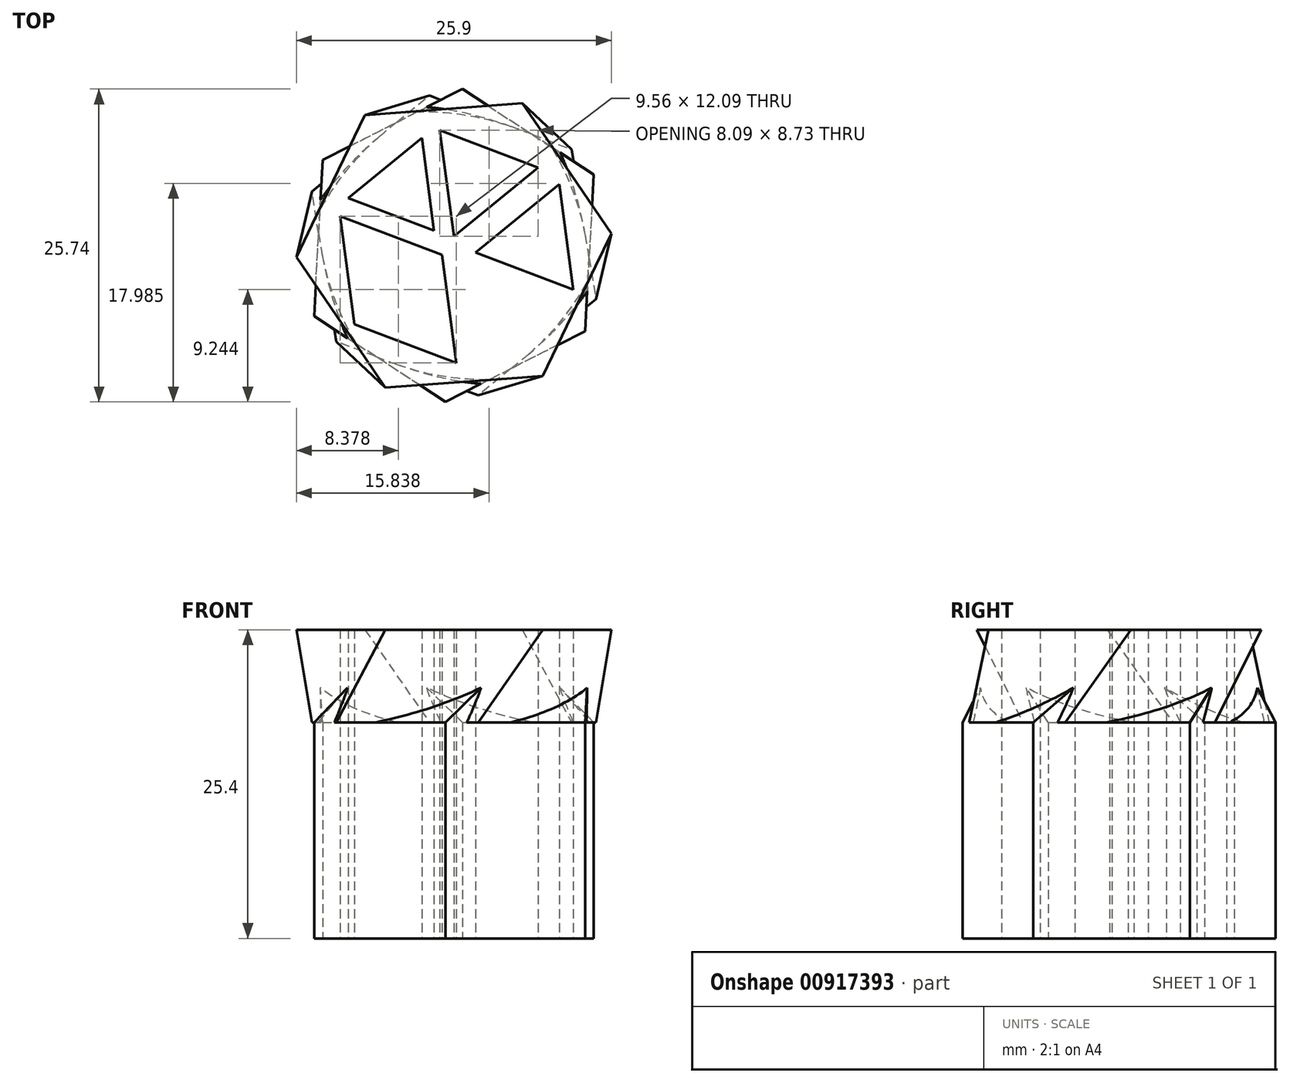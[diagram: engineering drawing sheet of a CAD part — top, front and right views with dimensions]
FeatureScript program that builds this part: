
annotation { "Feature Type Name" : "Feature", "Feature Type Description" : "" }
export const myFeature = defineFeature(function(context is Context, id is Id, definition is map)
    precondition{}
    {
        {
            var Q0;
            Q0=qCreatedBy(makeId("Top.planeOp"),FACE);
            cPlane(context, id + "F0", {"entities" : qUnion([Q0]), "cplaneType" : CPlaneType.OFFSET, "offset" : 7.62 * mm, "width" : 152.4 * mm, "height" : 152.4 * mm});
        }
        {
            var Q0;
            Q0=qCreatedBy(makeId("Top.planeOp"),FACE);
            var sketch = newSketch(context, id + "F1", { "sketchPlane" : qUnion([Q0])});
            skCircle(sketch, "E0.cCircle", {"center": v(0, 0) * mm, "radius": 10.82 * mm, "construction": true});
            skLineSegment(sketch, "E0.0", {"start": v(-11.68, 4.43) * mm, "end": v(-2, 12.33) * mm});
            skLineSegment(sketch, "E0.1", {"start": v(-2, 12.33) * mm, "end": v(9.68, 7.9) * mm});
            skLineSegment(sketch, "E0.2", {"start": v(9.68, 7.9) * mm, "end": v(11.68, -4.43) * mm});
            skLineSegment(sketch, "E0.3", {"start": v(11.68, -4.43) * mm, "end": v(2, -12.33) * mm});
            skLineSegment(sketch, "E0.4", {"start": v(2, -12.33) * mm, "end": v(-9.68, -7.9) * mm});
            skLineSegment(sketch, "E0.5", {"start": v(-9.68, -7.9) * mm, "end": v(-11.68, 4.43) * mm});
            skPoint(sketch, "E0.0.midPoint", {"position": v(-6.84, 8.38) * mm});
            skSolve(sketch);
        }
        {
            var Q0;
            Q0=qCreatedBy(id+"F0.planeOp",FACE);
            var sketch = newSketch(context, id + "F2", { "sketchPlane" : qUnion([Q0])});
            skCircle(sketch, "E1.cCircle", {"center": v(0, 0) * mm, "radius": 11.24 * mm, "construction": true});
            skLineSegment(sketch, "E1.0", {"start": v(5.63, 11.7) * mm, "end": v(12.95, 0.97) * mm});
            skLineSegment(sketch, "E1.1", {"start": v(12.95, 0.97) * mm, "end": v(7.31, -10.73) * mm});
            skLineSegment(sketch, "E1.2", {"start": v(7.31, -10.73) * mm, "end": v(-5.63, -11.7) * mm});
            skLineSegment(sketch, "E1.3", {"start": v(-5.63, -11.7) * mm, "end": v(-12.95, -0.97) * mm});
            skLineSegment(sketch, "E1.4", {"start": v(-12.95, -0.97) * mm, "end": v(-7.31, 10.73) * mm});
            skLineSegment(sketch, "E1.5", {"start": v(-7.31, 10.73) * mm, "end": v(5.63, 11.7) * mm});
            skPoint(sketch, "E1.0.midPoint", {"position": v(9.3, 6.33) * mm});
            skSolve(sketch);
        }
        {
            var Q0;
            Q0=makeQuery(id+"F2.imprint","IMPRINT",FACE,{"disambiguationData":[TD([[makeQuery(id+"F2.imprint","IMPRINT",EDGE,{"derivedFrom":sQuery(id+"F2.wireOp",EDGE,"E1.0")}),-1.0]])]});
            var Q1;
            Q1=makeQuery(id+"F1.imprint","IMPRINT",FACE,{"disambiguationData":[TD([[makeQuery(id+"F1.imprint","IMPRINT",EDGE,{"derivedFrom":sQuery(id+"F1.wireOp",EDGE,"E0.0")}),-1.0]])]});
            loft(context, id + "F3", {"sheetProfilesArray" : [{ "sheetProfileEntities" : qUnion([Q0]) }, { "sheetProfileEntities" : qUnion([Q1]) }]});
        }
        {
            var Q0;
            Q0=makeQuery(id+"F1.imprint","IMPRINT",FACE,{"disambiguationData":[TD([[makeQuery(id+"F1.imprint","IMPRINT",EDGE,{"derivedFrom":sQuery(id+"F1.wireOp",EDGE,"E0.0")}),-1.0]])]});
            var sketch = newSketch(context, id + "F4", { "sketchPlane" : qUnion([Q0])});
            skLineSegment(sketch, "E2", {"start": v(-8.17, -6.5) * mm, "end": v(1.78, -10.27) * mm, "construction": true});
            skLineSegment(sketch, "E3", {"start": v(1.78, -10.27) * mm, "end": v(9.82, -3.7) * mm, "construction": true});
            skLineSegment(sketch, "E4", {"start": v(9.82, -3.7) * mm, "end": v(8.56, 5.8) * mm, "construction": true});
            skLineSegment(sketch, "E5", {"start": v(8.56, 5.8) * mm, "end": v(-1.65, 9.67) * mm, "construction": true});
            skLineSegment(sketch, "E6", {"start": v(-1.65, 9.67) * mm, "end": v(-9.47, 3.28) * mm, "construction": true});
            skLineSegment(sketch, "E7", {"start": v(-9.47, 3.28) * mm, "end": v(-8.17, -6.5) * mm, "construction": true});
            skLineSegment(sketch, "E8", {"start": v(-9.35, 2.42) * mm, "end": v(-0.97, -0.76) * mm});
            skLineSegment(sketch, "E9", {"start": v(-0.97, -0.76) * mm, "end": v(0.2, -9.67) * mm});
            skLineSegment(sketch, "E10", {"start": v(-9.35, 2.42) * mm, "end": v(-8.17, -6.5) * mm});
            skLineSegment(sketch, "E11", {"start": v(0.2, -9.67) * mm, "end": v(-8.17, -6.5) * mm});
            skLineSegment(sketch, "E12", {"start": v(-8.7, 3.9) * mm, "end": v(-1.63, 1.22) * mm});
            skLineSegment(sketch, "E13", {"start": v(-1.63, 1.22) * mm, "end": v(-2.64, 8.85) * mm});
            skLineSegment(sketch, "E14", {"start": v(-2.64, 8.85) * mm, "end": v(-8.7, 3.9) * mm});
            skLineSegment(sketch, "E15", {"start": v(6.93, 6.41) * mm, "end": v(0, 0.75) * mm});
            skLineSegment(sketch, "E16", {"start": v(0, 0.75) * mm, "end": v(-1.16, 9.48) * mm});
            skLineSegment(sketch, "E17", {"start": v(-1.16, 9.48) * mm, "end": v(6.93, 6.41) * mm});
            skLineSegment(sketch, "E18", {"start": v(8.66, 5.03) * mm, "end": v(1.78, -0.59) * mm});
            skLineSegment(sketch, "E19", {"start": v(1.78, -0.59) * mm, "end": v(9.8, -3.63) * mm});
            skLineSegment(sketch, "E20", {"start": v(9.8, -3.63) * mm, "end": v(8.66, 5.03) * mm});
            skLineSegment(sketch, "E21", {"start": v(0.66, -1.8) * mm, "end": v(1.78, -10.27) * mm});
            skLineSegment(sketch, "E22", {"start": v(1.78, -10.27) * mm, "end": v(0.66, -1.8) * mm});
            skLineSegment(sketch, "E23", {"start": v(0.66, -1.8) * mm, "end": v(8.51, -4.77) * mm});
            skLineSegment(sketch, "E24", {"start": v(8.51, -4.77) * mm, "end": v(1.78, -10.27) * mm});
            skSolve(sketch);
        }
        {
            var Q0;
            Q0=makeQuery(id+"F4.imprint","IMPRINT",FACE,{"disambiguationData":[TD([[makeQuery(id+"F4.imprint","IMPRINT",EDGE,{"derivedFrom":sQuery(id+"F4.wireOp",EDGE,"E22")}),-1.0]])]});
            var Q1;
            Q1=makeQuery(id+"F4.imprint","IMPRINT",FACE,{"disambiguationData":[TD([[makeQuery(id+"F4.imprint","IMPRINT",EDGE,{"derivedFrom":sQuery(id+"F4.wireOp",EDGE,"E8")}),-1.0]])]});
            var Q2;
            Q2=makeQuery(id+"F4.imprint","IMPRINT",FACE,{"disambiguationData":[TD([[makeQuery(id+"F4.imprint","IMPRINT",EDGE,{"derivedFrom":sQuery(id+"F4.wireOp",EDGE,"E12")}),1.0]])]});
            var Q3;
            Q3=makeQuery(id+"F4.imprint","IMPRINT",FACE,{"disambiguationData":[TD([[makeQuery(id+"F4.imprint","IMPRINT",EDGE,{"derivedFrom":sQuery(id+"F4.wireOp",EDGE,"E15")}),-1.0]])]});
            var Q4;
            Q4=makeQuery(id+"F4.imprint","IMPRINT",FACE,{"disambiguationData":[TD([[makeQuery(id+"F4.imprint","IMPRINT",EDGE,{"derivedFrom":sQuery(id+"F4.wireOp",EDGE,"E18")}),1.0]])]});
            extrude(context, id + "F5", {"entities" : qUnion([Q0, Q1, Q2, Q3, Q4]), "operationType" : NewBodyOperationType.REMOVE, "endBound" : BoundingType.THROUGH_ALL, "depth" : 25.4 * mm, "offsetDistance" : 25.4 * mm});
        }
        {
            var Q0;
            Q0=qCreatedBy(makeId("Top.planeOp"),FACE);
            cPlane(context, id + "F6", {"entities" : qUnion([Q0]), "cplaneType" : CPlaneType.OFFSET, "offset" : 17.78 * mm, "oppositeDirection" : true, "width" : 152.4 * mm, "height" : 152.4 * mm});
        }
        {
            var Q0;
            Q0=qCreatedBy(id+"F6.planeOp",FACE);
            var sketch = newSketch(context, id + "F7", { "sketchPlane" : qUnion([Q0])});
            skCircle(sketch, "E25.cCircle", {"center": v(0, 0) * mm, "radius": 11.17 * mm, "construction": true});
            skLineSegment(sketch, "E25.0", {"start": v(-10.8, 7.05) * mm, "end": v(0.7, 12.87) * mm});
            skLineSegment(sketch, "E25.1", {"start": v(0.7, 12.87) * mm, "end": v(11.5, 5.83) * mm});
            skLineSegment(sketch, "E25.2", {"start": v(11.5, 5.83) * mm, "end": v(10.8, -7.05) * mm});
            skLineSegment(sketch, "E25.3", {"start": v(10.8, -7.05) * mm, "end": v(-0.7, -12.87) * mm});
            skLineSegment(sketch, "E25.4", {"start": v(-0.7, -12.87) * mm, "end": v(-11.5, -5.83) * mm});
            skLineSegment(sketch, "E25.5", {"start": v(-11.5, -5.83) * mm, "end": v(-10.8, 7.05) * mm});
            skPoint(sketch, "E25.0.midPoint", {"position": v(-5.05, 9.96) * mm});
            skSolve(sketch);
        }
        {
            var Q0;
            Q0=makeQuery(id+"F7.imprint","IMPRINT",FACE,{"disambiguationData":[TD([[makeQuery(id+"F7.imprint","IMPRINT",EDGE,{"derivedFrom":sQuery(id+"F7.wireOp",EDGE,"E25.0")}),-1.0]])]});
            extrude(context, id + "F8", {"entities" : qUnion([Q0]), "operationType" : NewBodyOperationType.ADD, "depth" : 22.86 * mm, "offsetDistance" : 25.4 * mm});
        }
        {
            var Q0;
            Q0=makeQuery(id+"F8.boolean.opBoolean","SPLIT",FACE,{"disambiguationData":[TD([makeQuery(id+"F5.boolean.opBoolean","COPY",FACE,{"derivedFrom":makeQuery(id+"F5.opExtrude","SWEPT_FACE",FACE,{"disambiguationData":[OSD([sQuery(id+"F4.wireOp",EDGE,"E8")])]})})])],"derivedFrom":makeQuery(id+"F8.opExtrude","CAP_FACE",FACE,{"disambiguationData":[OSD([sQuery(id+"F7.wireOp",EDGE,"E25.0"),sQuery(id+"F7.wireOp",EDGE,"E25.1"),sQuery(id+"F7.wireOp",EDGE,"E25.2"),sQuery(id+"F7.wireOp",EDGE,"E25.3"),sQuery(id+"F7.wireOp",EDGE,"E25.4"),sQuery(id+"F7.wireOp",EDGE,"E25.5")])],"isStart":false})});
            var Q1;
            Q1=makeQuery(id+"F8.boolean.opBoolean","SPLIT",FACE,{"disambiguationData":[TD([makeQuery(id+"F5.boolean.opBoolean","COPY",FACE,{"derivedFrom":makeQuery(id+"F5.opExtrude","SWEPT_FACE",FACE,{"disambiguationData":[OSD([sQuery(id+"F4.wireOp",EDGE,"E12")])]})})])],"derivedFrom":makeQuery(id+"F8.opExtrude","CAP_FACE",FACE,{"disambiguationData":[OSD([sQuery(id+"F7.wireOp",EDGE,"E25.0"),sQuery(id+"F7.wireOp",EDGE,"E25.1"),sQuery(id+"F7.wireOp",EDGE,"E25.2"),sQuery(id+"F7.wireOp",EDGE,"E25.3"),sQuery(id+"F7.wireOp",EDGE,"E25.4"),sQuery(id+"F7.wireOp",EDGE,"E25.5")])],"isStart":false})});
            var Q2;
            Q2=makeQuery(id+"F8.boolean.opBoolean","SPLIT",FACE,{"disambiguationData":[TD([makeQuery(id+"F5.boolean.opBoolean","COPY",FACE,{"derivedFrom":makeQuery(id+"F5.opExtrude","SWEPT_FACE",FACE,{"disambiguationData":[OSD([sQuery(id+"F4.wireOp",EDGE,"E15")])]})})])],"derivedFrom":makeQuery(id+"F8.opExtrude","CAP_FACE",FACE,{"disambiguationData":[OSD([sQuery(id+"F7.wireOp",EDGE,"E25.0"),sQuery(id+"F7.wireOp",EDGE,"E25.1"),sQuery(id+"F7.wireOp",EDGE,"E25.2"),sQuery(id+"F7.wireOp",EDGE,"E25.3"),sQuery(id+"F7.wireOp",EDGE,"E25.4"),sQuery(id+"F7.wireOp",EDGE,"E25.5")])],"isStart":false})});
            var Q3;
            Q3=makeQuery(id+"F8.boolean.opBoolean","SPLIT",FACE,{"disambiguationData":[TD([makeQuery(id+"F5.boolean.opBoolean","COPY",FACE,{"derivedFrom":makeQuery(id+"F5.opExtrude","SWEPT_FACE",FACE,{"disambiguationData":[OSD([sQuery(id+"F4.wireOp",EDGE,"E18")])]})})])],"derivedFrom":makeQuery(id+"F8.opExtrude","CAP_FACE",FACE,{"disambiguationData":[OSD([sQuery(id+"F7.wireOp",EDGE,"E25.0"),sQuery(id+"F7.wireOp",EDGE,"E25.1"),sQuery(id+"F7.wireOp",EDGE,"E25.2"),sQuery(id+"F7.wireOp",EDGE,"E25.3"),sQuery(id+"F7.wireOp",EDGE,"E25.4"),sQuery(id+"F7.wireOp",EDGE,"E25.5")])],"isStart":false})});
            var Q4;
            Q4=makeQuery(id+"F8.boolean.opBoolean","SPLIT",FACE,{"disambiguationData":[TD([makeQuery(id+"F5.boolean.opBoolean","COPY",FACE,{"derivedFrom":makeQuery(id+"F5.opExtrude","SWEPT_FACE",FACE,{"disambiguationData":[OSD([sQuery(id+"F4.wireOp",EDGE,"E22")])]})})])],"derivedFrom":makeQuery(id+"F8.opExtrude","CAP_FACE",FACE,{"disambiguationData":[OSD([sQuery(id+"F7.wireOp",EDGE,"E25.0"),sQuery(id+"F7.wireOp",EDGE,"E25.1"),sQuery(id+"F7.wireOp",EDGE,"E25.2"),sQuery(id+"F7.wireOp",EDGE,"E25.3"),sQuery(id+"F7.wireOp",EDGE,"E25.4"),sQuery(id+"F7.wireOp",EDGE,"E25.5")])],"isStart":false})});
            extrude(context, id + "F9", {"entities" : qUnion([Q0, Q1, Q2, Q3, Q4]), "operationType" : NewBodyOperationType.REMOVE, "endBound" : BoundingType.THROUGH_ALL, "oppositeDirection" : true, "depth" : 25.4 * mm, "offsetDistance" : 25.4 * mm});
        }
        {
            var Q0;
            {var subQ0=sQuery(id+"F7.wireOp",EDGE,"E25.1");var subQ1=sQuery(id+"F7.wireOp",EDGE,"E25.2");Q0=makeQuery(id+"F8.boolean.opBoolean","SPLIT",EDGE,{"disambiguationData":[TD([makeQuery(id+"F8.opExtrude","SWEPT_FACE",FACE,{"disambiguationData":[OSD([subQ0])]})])],"derivedFrom":makeQuery(id+"F8.opExtrude","CAP_EDGE",EDGE,{"disambiguationData":[OSD([subQ1])],"isStart":false})});}
            var Q1;
            {var subQ0=sQuery(id+"F7.wireOp",EDGE,"E25.1");var subQ1=sQuery(id+"F7.wireOp",EDGE,"E25.0");Q1=makeQuery(id+"F8.boolean.opBoolean","SPLIT",EDGE,{"disambiguationData":[TD([makeQuery(id+"F8.opExtrude","SWEPT_FACE",FACE,{"disambiguationData":[OSD([subQ1])]})])],"derivedFrom":makeQuery(id+"F8.opExtrude","CAP_EDGE",EDGE,{"disambiguationData":[OSD([subQ0])],"isStart":false})});}
            var Q2;
            {var subQ0=sQuery(id+"F7.wireOp",EDGE,"E25.0");var subQ1=sQuery(id+"F7.wireOp",EDGE,"E25.5");Q2=makeQuery(id+"F8.boolean.opBoolean","SPLIT",EDGE,{"disambiguationData":[TD([makeQuery(id+"F8.opExtrude","SWEPT_FACE",FACE,{"disambiguationData":[OSD([subQ1])]})])],"derivedFrom":makeQuery(id+"F8.opExtrude","CAP_EDGE",EDGE,{"disambiguationData":[OSD([subQ0])],"isStart":false})});}
            var Q3;
            {var subQ0=sQuery(id+"F7.wireOp",EDGE,"E25.2");var subQ1=sQuery(id+"F7.wireOp",EDGE,"E25.3");Q3=makeQuery(id+"F8.boolean.opBoolean","SPLIT",EDGE,{"disambiguationData":[TD([makeQuery(id+"F8.opExtrude","SWEPT_FACE",FACE,{"disambiguationData":[OSD([subQ0])]})])],"derivedFrom":makeQuery(id+"F8.opExtrude","CAP_EDGE",EDGE,{"disambiguationData":[OSD([subQ1])],"isStart":false})});}
            var Q4;
            {var subQ0=sQuery(id+"F7.wireOp",EDGE,"E25.3");var subQ1=sQuery(id+"F7.wireOp",EDGE,"E25.4");Q4=makeQuery(id+"F8.boolean.opBoolean","SPLIT",EDGE,{"disambiguationData":[TD([makeQuery(id+"F8.opExtrude","SWEPT_FACE",FACE,{"disambiguationData":[OSD([subQ0])]})])],"derivedFrom":makeQuery(id+"F8.opExtrude","CAP_EDGE",EDGE,{"disambiguationData":[OSD([subQ1])],"isStart":false})});}
            var Q5;
            {var subQ0=sQuery(id+"F7.wireOp",EDGE,"E25.4");var subQ1=sQuery(id+"F7.wireOp",EDGE,"E25.5");Q5=makeQuery(id+"F8.boolean.opBoolean","SPLIT",EDGE,{"disambiguationData":[TD([makeQuery(id+"F8.opExtrude","SWEPT_FACE",FACE,{"disambiguationData":[OSD([subQ0])]})])],"derivedFrom":makeQuery(id+"F8.opExtrude","CAP_EDGE",EDGE,{"disambiguationData":[OSD([subQ1])],"isStart":false})});}
            chamfer(context, id + "F10", {"entities" : qUnion([Q0, Q1, Q2, Q3, Q4, Q5]), "width" : 5.08 * mm, "tangentPropagation" : true});
        }
    });
